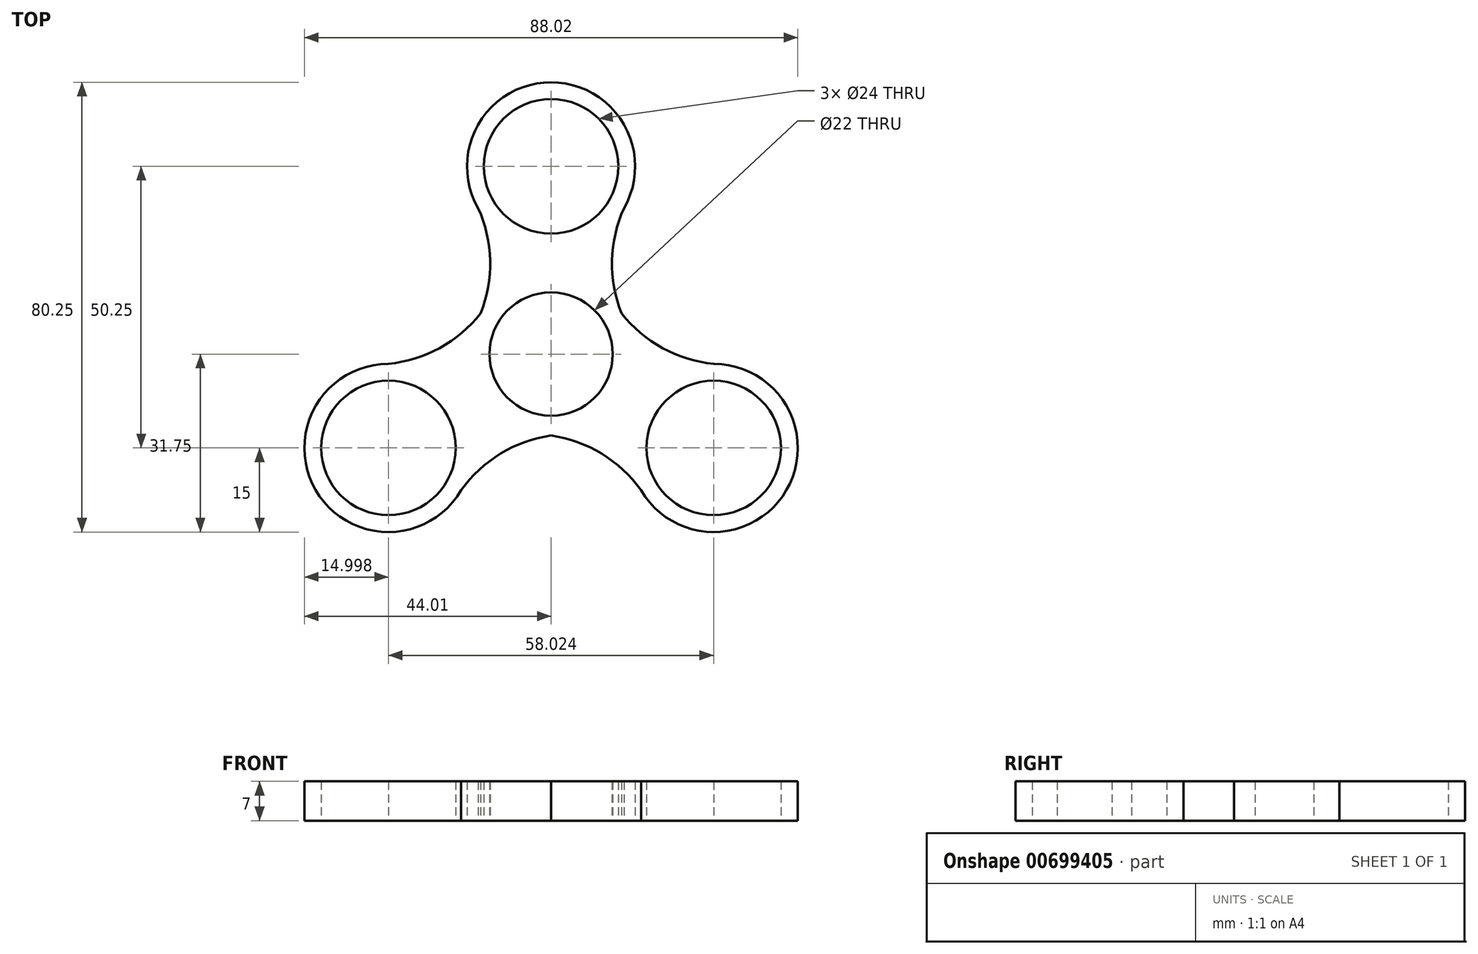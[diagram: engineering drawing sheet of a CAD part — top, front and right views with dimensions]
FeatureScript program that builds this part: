
annotation { "Feature Type Name" : "Feature", "Feature Type Description" : "" }
export const myFeature = defineFeature(function(context is Context, id is Id, definition is map)
    precondition{}
    {
        {
            var Q0;
            Q0=qCreatedBy(makeId("Top.planeOp"),FACE);
            var sketch = newSketch(context, id + "F0", { "sketchPlane" : qUnion([Q0])});
            skCircle(sketch, "E0", {"center": v(0, 0) * mm, "radius": 11 * mm});
            skCircle(sketch, "E1", {"center": v(0, 0) * mm, "radius": 14.5 * mm});
            skCircle(sketch, "E2", {"center": v(0, 0) * mm, "radius": 48.5 * mm, "construction": true});
            skCircle(sketch, "E3", {"center": v(0, 33.5) * mm, "radius": 12 * mm});
            skCircle(sketch, "E4", {"center": v(0, 33.5) * mm, "radius": 15 * mm});
            skCircle(sketch, "E5.1.0", {"center": v(-29.01, -16.75) * mm, "radius": 15 * mm});
            skCircle(sketch, "E5.1.1", {"center": v(-29.01, -16.75) * mm, "radius": 12 * mm});
            skArc(sketch, "E5.1.3", {"start": v(0, -14.52) * mm, "mid": v(-9.01, -17.77) * mm, "end": v(-16.04, -24.28) * mm});
            skCircle(sketch, "E5.2.0", {"center": v(29.01, -16.75) * mm, "radius": 15 * mm});
            skCircle(sketch, "E5.2.1", {"center": v(29.01, -16.75) * mm, "radius": 12 * mm});
            skArc(sketch, "E5.2.2", {"start": v(0, -14.52) * mm, "mid": v(9.01, -17.77) * mm, "end": v(16.04, -24.28) * mm});
            skPoint(sketch, "E6", {"position": v(-12.58, 7.26) * mm});
            skArc(sketch, "E7.trimOffspring", {"start": v(-12.58, 7.26) * mm, "mid": v(-19.9, 1.08) * mm, "end": v(-29.05, -1.75) * mm});
            skArc(sketch, "E8.trimOffspring", {"start": v(-12.58, 7.26) * mm, "mid": v(-10.88, 16.69) * mm, "end": v(-13, 26.03) * mm});
            skPoint(sketch, "E9.start.orphan", {"position": v(-13.6, 5.04) * mm});
            skPoint(sketch, "E10", {"position": v(12.58, 7.26) * mm});
            skArc(sketch, "E11.trimOffspring", {"start": v(12.58, 7.26) * mm, "mid": v(19.9, 1.08) * mm, "end": v(29.05, -1.75) * mm});
            skArc(sketch, "E12.trimOffspring", {"start": v(12.58, 7.26) * mm, "mid": v(10.88, 16.69) * mm, "end": v(13, 26.03) * mm});
            skPoint(sketch, "E13.MirrorCS.start.orphan", {"position": v(13.6, 5.04) * mm});
            skPoint(sketch, "E14", {"position": v(0, -14.52) * mm});
            skPoint(sketch, "E15.orphan", {"position": v(-2.43, -14.3) * mm});
            skPoint(sketch, "E16.orphan", {"position": v(2.43, -14.3) * mm});
            skSolve(sketch);
        }
        {
            var Q0;
            Q0=qSketchRegion(id+"F0",true);
            var Q1;
            Q1=makeQuery(id+"F0.imprint","IMPRINT",FACE,{"disambiguationData":[TD([[makeQuery(id+"F0.imprint","IMPRINT",EDGE,{"derivedFrom":sQuery(id+"F0.wireOp",EDGE,"E0")}),-1.0]])]});
            extrude(context, id + "F1", {"entities" : qUnion([Q0, Q1]), "depth" : 7 * mm, "offsetDistance" : 25 * mm});
        }
    });
